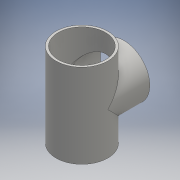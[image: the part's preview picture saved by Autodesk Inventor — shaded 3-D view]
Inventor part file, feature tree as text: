
AUTODESK INVENTOR PART (.ipt)
format: ipt  version: 2016 (Build 200138000, 138)  size: 147,456 bytes
history: native  units: mm
features: extrude x4, sketch x4, projected_geometry x1
ambient origin geometry x8: Origin, YZ Plane, XZ Plane, XY Plane, X Axis, Y Axis, Z Axis, Center Point
bodies: Solid1 (feature_tree)
feature tree (9):
  extrude  "Extrusion1"  Depth=9.52mm
  extrude  "Extrusion2"  Depth=9.52mm
  extrude  "Extrusion3"  Depth=178.0mm TaperAngle=0.0deg
  extrude  "Extrusion4"  Depth=178.0mm TaperAngle=0.0deg
  sketch  "Sketch1"  dims[d0=219.0mm d1=9.52mm]
  sketch  "Sketch2"  dims[d2=356.0mm d3=0.0mm d4=9.52mm]
  sketch  "Sketch3"  dims[d5=219.0mm d6=178.0mm d7=0.0mm]
  sketch  "Sketch4"  dims[d8=254.0mm d9=0.0mm d10=178.0mm d11=0.0mm]
  projected_geometry  "Projected Loop1"
